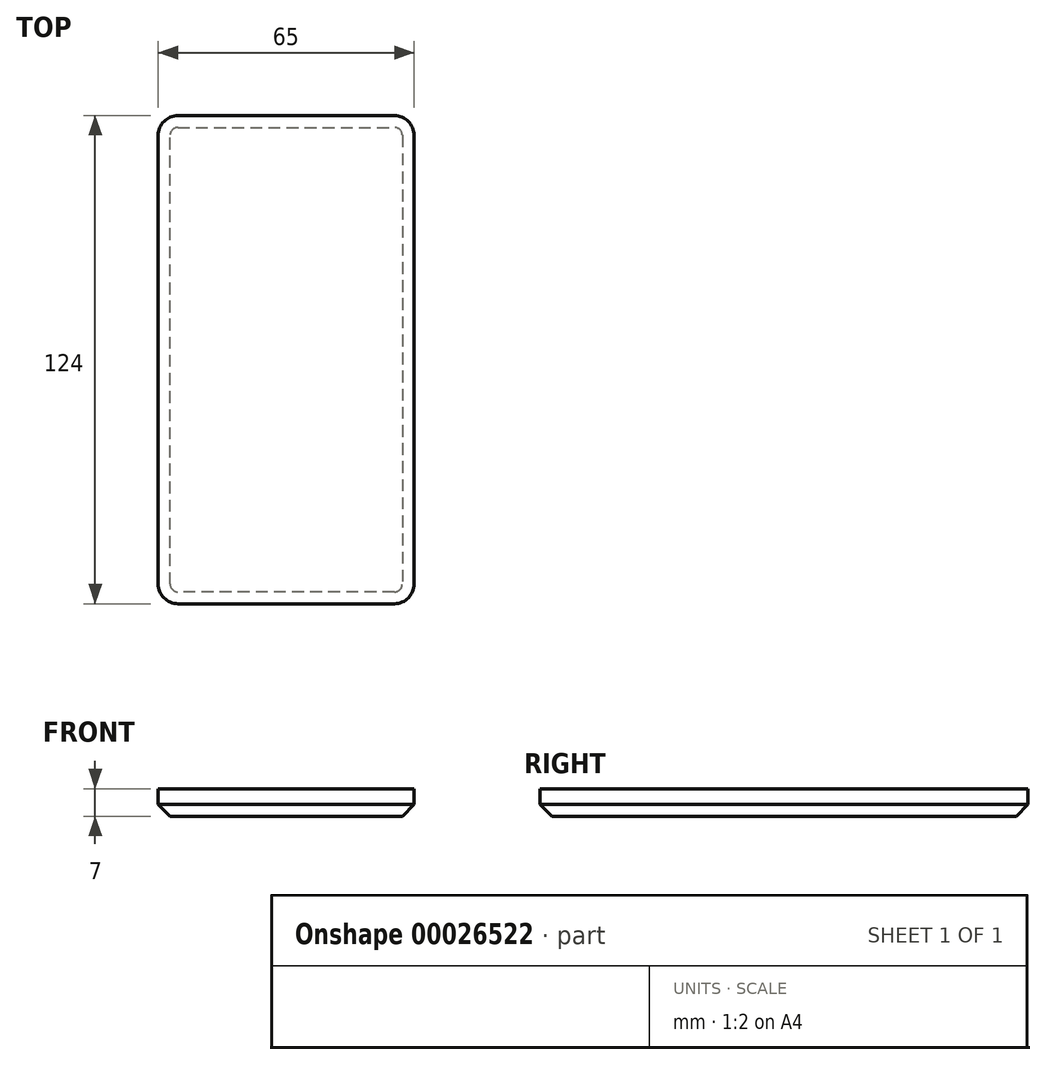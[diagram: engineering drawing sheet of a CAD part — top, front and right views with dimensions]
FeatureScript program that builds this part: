
annotation { "Feature Type Name" : "Feature", "Feature Type Description" : "" }
export const myFeature = defineFeature(function(context is Context, id is Id, definition is map)
    precondition{}
    {
        {
            var Q0;
            Q0=qCreatedBy(makeId("Top.planeOp"),FACE);
            var sketch = newSketch(context, id + "F0", { "sketchPlane" : qUnion([Q0])});
            skLineSegment(sketch, "E0.rect.bottom", {"start": v(32.5, 62) * mm, "end": v(-32.5, 62) * mm});
            skLineSegment(sketch, "E0.rect.top", {"start": v(32.5, -62) * mm, "end": v(-32.5, -62) * mm});
            skLineSegment(sketch, "E0.rect.left", {"start": v(32.5, 62) * mm, "end": v(32.5, -62) * mm});
            skLineSegment(sketch, "E0.rect.right", {"start": v(-32.5, 62) * mm, "end": v(-32.5, -62) * mm});
            skPoint(sketch, "E0.rect.middle", {"position": v(0, 0) * mm});
            skSolve(sketch);
        }
        {
            var Q0;
            Q0=makeQuery(id+"F0.imprint","IMPRINT",FACE,{"disambiguationData":[TD([[makeQuery(id+"F0.imprint","IMPRINT",EDGE,{"derivedFrom":sQuery(id+"F0.wireOp",EDGE,"E0.rect.bottom")}),1.0]])]});
            extrude(context, id + "F1", {"entities" : qUnion([Q0]), "depth" : 7 * mm});
        }
        {
            var Q0;
            Q0=makeQuery(id+"F1.opExtrude","SWEPT_EDGE",EDGE,{"disambiguationData":[OSD([sQuery(id+"F0.wireOp",EDGE,"E0.rect.top"),sQuery(id+"F0.wireOp",EDGE,"E0.rect.left")])]});
            var Q1;
            Q1=makeQuery(id+"F1.opExtrude","SWEPT_EDGE",EDGE,{"disambiguationData":[OSD([sQuery(id+"F0.wireOp",EDGE,"E0.rect.bottom"),sQuery(id+"F0.wireOp",EDGE,"E0.rect.left")])]});
            var Q2;
            Q2=makeQuery(id+"F1.opExtrude","SWEPT_EDGE",EDGE,{"disambiguationData":[OSD([sQuery(id+"F0.wireOp",EDGE,"E0.rect.top"),sQuery(id+"F0.wireOp",EDGE,"E0.rect.right")])]});
            var Q3;
            Q3=makeQuery(id+"F1.opExtrude","SWEPT_EDGE",EDGE,{"disambiguationData":[OSD([sQuery(id+"F0.wireOp",EDGE,"E0.rect.bottom"),sQuery(id+"F0.wireOp",EDGE,"E0.rect.right")])]});
            fillet(context, id + "F2", {"entities" : qUnion([Q0, Q1, Q2, Q3]), "radius" : 5 * mm, "tangentPropagation" : true, "allowEdgeOverflow" : false});
        }
        {
            var Q0;
            Q0=makeQuery(id+"F1.opExtrude","CAP_FACE",FACE,{"disambiguationData":[OSD([sQuery(id+"F0.wireOp",EDGE,"E0.rect.bottom"),sQuery(id+"F0.wireOp",EDGE,"E0.rect.top"),sQuery(id+"F0.wireOp",EDGE,"E0.rect.left"),sQuery(id+"F0.wireOp",EDGE,"E0.rect.right")])],"isStart":true});
            chamfer(context, id + "F3", {"entities" : qUnion([Q0]), "width" : 3 * mm, "tangentPropagation" : true});
        }
    });
